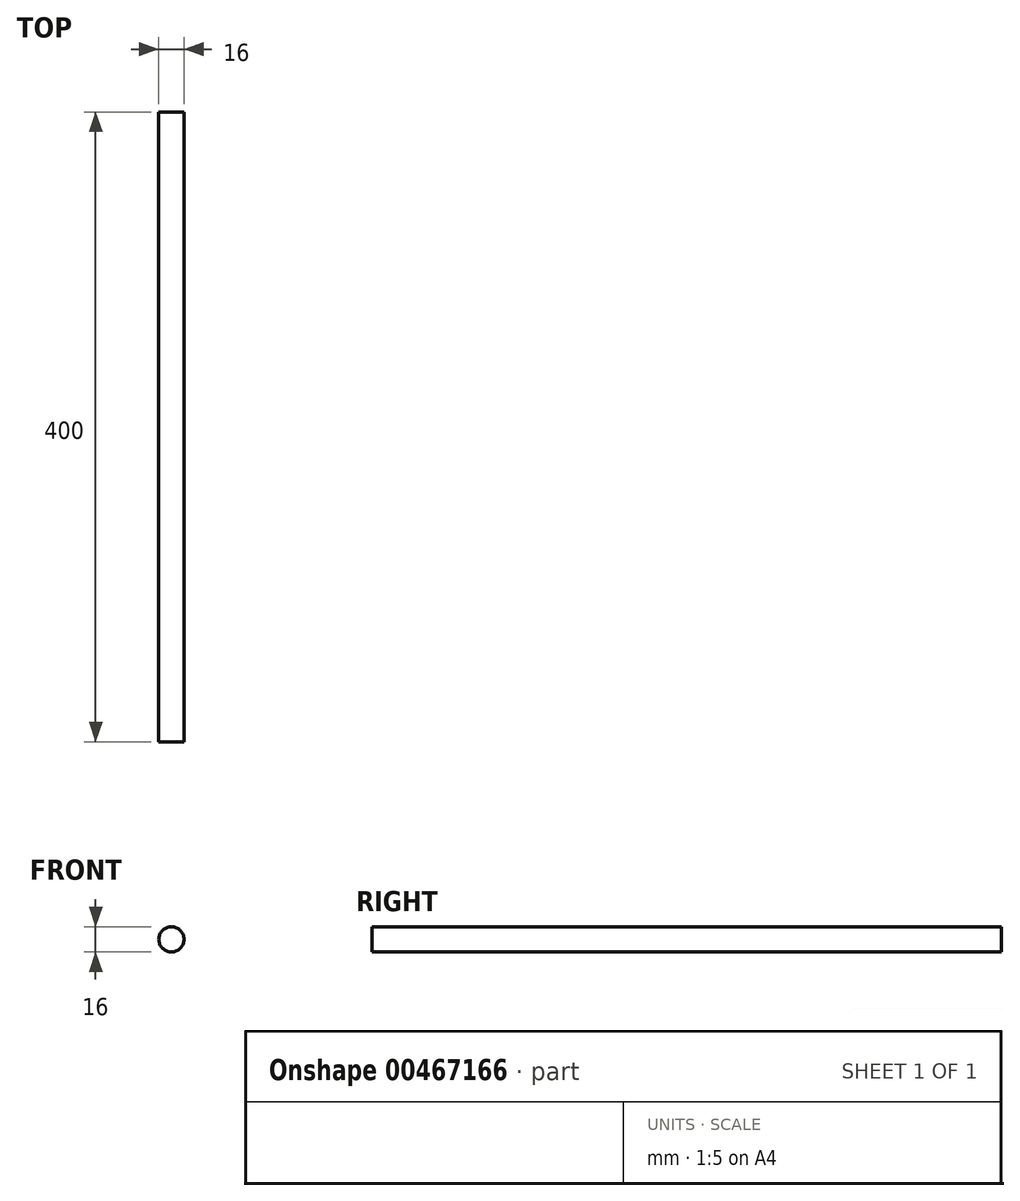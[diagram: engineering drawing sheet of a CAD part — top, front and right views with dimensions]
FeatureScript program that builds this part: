
annotation { "Feature Type Name" : "Feature", "Feature Type Description" : "" }
export const myFeature = defineFeature(function(context is Context, id is Id, definition is map)
    precondition{}
    {
        {
            assignVariable(context, id + "F0", {"name" : "Shaft_length", "anyValue" : 400 * mm});
        }
        {
            var Q0;
            Q0=qCreatedBy(makeId("Front.planeOp"),FACE);
            var sketch = newSketch(context, id + "F1", { "sketchPlane" : qUnion([Q0])});
            skCircle(sketch, "E0", {"center": v(0, 0) * mm, "radius": 8 * mm});
            skSolve(sketch);
        }
        {
            var Q0;
            Q0 = qSketchRegion(id + "F1", true);
            extrude(context, id + "F2", {"entities" : qUnion([Q0]), "oppositeDirection" : true, "depth" : getVariable(context, 'Shaft_length')});
        }
    });
